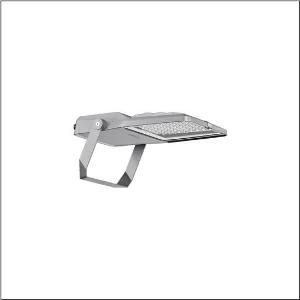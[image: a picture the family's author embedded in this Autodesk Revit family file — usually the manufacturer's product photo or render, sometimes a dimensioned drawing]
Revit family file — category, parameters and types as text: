
# Revit family: floodlight_fl_21_iq_mini___pl52_5xa7771b4d1a_5516
name_source: partatom
category: Lighting Fixtures
units: mm (PartAtom-declared; Revit-internal decimal feet)

## family parameters
Cut with Voids When Loaded = No
Host = Face
Light Source = No
Part Type = Normal
Room Calculation Point = No
Round Connector Dimension = Use Diameter
Shared = No

## types (1)
- --- (1 x LED, 6490 lm, 45.5 W, 4000K)
    Apparent Load = 46 VA
    CIE Flux Codes = 26 60 98 100 100
    Color Rendering = 70
    Color Temperature = 4000K
    Default Elevation = 1800 mm
    Description = Floodlight FL 21 iQ mini, floodlight, primary light control with lens, of PMMA, primary optical cover: protective disc, of toughened safety glass, transparent, light distribution: PL52, light emission: direct distribution, installation type: surface-mounted, LED, High Power LED, rated luminous flux: 6.490lm, luminous efficacy: 143lm/W, light colour: 740, colour temperature: 4000K, control: Auto-Match, Temp-Guard, Lumen-Switch, Night-Set, Smart-Wire, Light-Fading, Desk-Remote (wireless, voltage-free reading and setting of iQ features in the workshop via application-optimized NFC function/RFID function), optimised constant luminous flux control (CLO 2.0), with terminal, 6-pole, mains connection: 220..240V, AC, 50/60Hz, start of lifetime: 46W, end of service life: 48W, reduction: 22W, luminaire housing, of diecast aluminium, powder-coated, Siteco® metallic grey (DB 702S), corrosivity category C5 mid according to DIN EN ISO 12944, sealing non-destructively replaceable, mounting bracket, of steel, galvanised, powder-coated, Siteco® metallic grey (DB 702S), protection rating (complete): IP66, insulation class (complete): insulation class II (safety insulation), certification: CE, ENEC, VDE, protection symbol: D, impact resistance: IK08, permissible operating ambient temperature: -40..+40°C, permissible operating ambient temperature for outdoor applications: -40..+50°C, standard: DIN EN 12944, LABS conformity tested according to VDMA 24364:2018-05, packaging unit: 1 piece

Light Distribution: PL52
    Height = 70 mm
    Lamp = 1 x LED
    Lamp Light Flux = 6490 lm
    Lamp Power = 45.5 W
    Lamp count = 1
    Length = 485 mm
    Luminous efficacy = 143 lm/W
    Manufacturer = Siteco
    ModVariant = No
    Model = 5XA7771B4D1A
    Mounting Place = Wall
    Mounting Type = Surface mounted
    Number of Poles = 1
    OnlyDefault = Yes
    Power Factor = 1
    Product Name = Floodlight FL 21 iQ mini | PL52
    Product group = floodlight | wall mounted
    ProductGroupID = 2001
    Protection Class = Protection class II
    Protection Degree = IP 66
    RLX_Detail_Level = 1
    RLX_Emergency_Light_Flux = 0 lm
    RLX_Emergency_Type = 0
    RLX_Emergency_Type_DB = No
    RlxData = <blob elided: 96377 chars, md5=5ca2351e>
    Socket = socket
    Standby Power = 0 W
    System Light Flux = 6490 lm
    System Power = 46 W
    Type Comments = factory setting: luminous flux: 100 % | dim-lin: 254 | 463 mA
    Type Image = l_1006845.jpg
    URL = http://relux.com
    VarID = @adj_097359
    Voltage = 0 V
    Weight = 0.00 kg
    Width = 337 mm

## geometry (parser evidence)
native form markers: Blend x4, Sweep x12
no freeform markers — native parametric forms only
